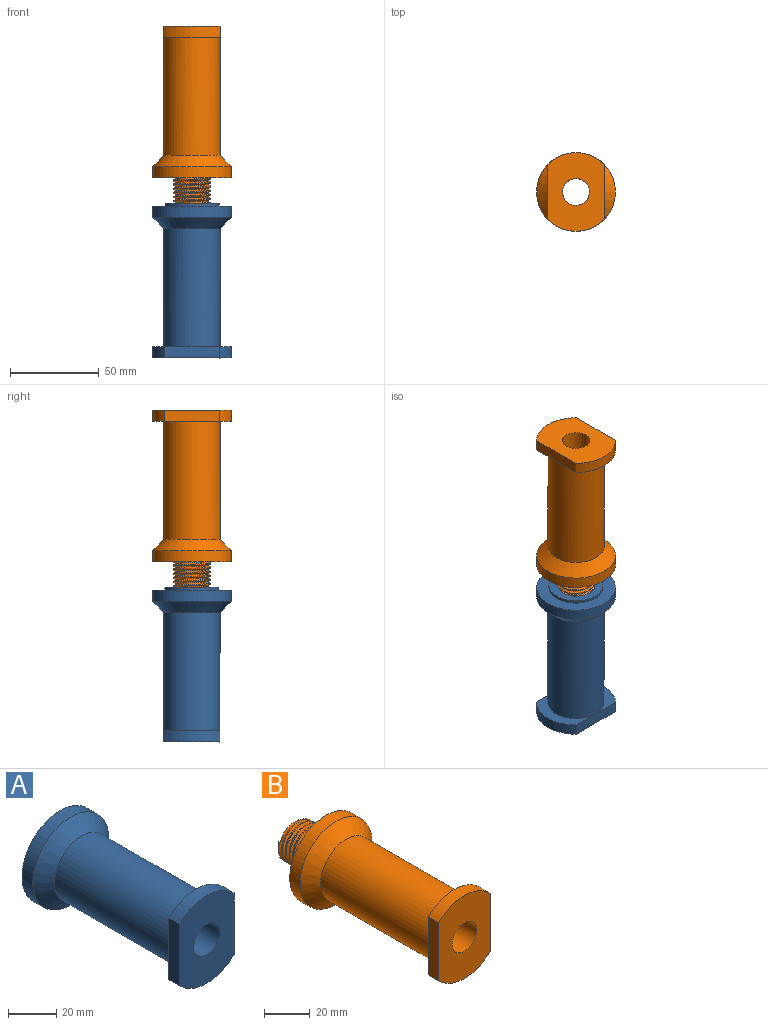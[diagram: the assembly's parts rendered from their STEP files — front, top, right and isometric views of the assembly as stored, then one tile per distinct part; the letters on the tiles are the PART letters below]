
ASSEMBLY  parts=2 mates=1
PART A: 34 faces, bbox 45x87.8x45 mm
  f0: plane 20.7x14.09mm, normal (0,1,0), area 25.9mm2, adj f1,f2,f3,f4,f17
  f1: bspline ~28.83x23.46mm, area 930.4mm2, adj f0,f2,f3,f5,f17,f18,f19,f20
  f2: plane 0.98x0.58mm, normal (0.98,0,0.17), area 0.3mm2, adj f0,f1,f17
  f3: cylinder r=9.06mm len=27.88mm, axis (0,1,0), area 343.1mm2, adj f0,f1,f4,f30
  f4: bspline ~28.07x23.46mm, area 907.7mm2, adj f0,f3,f17,f18,f19,f20,f21,f22
  f5: plane 20.32x20.32mm, normal (0,1,0), area 134.2mm2, adj f1,f7,f29,f30
  f6: cylinder r=15.88mm len=66.68mm, axis (0,1,0), area 6650.5mm2, adj f10,f11,f31
  f7: cylinder r=7.62mm len=57.79mm, axis (0,1,0), area 2766.6mm2, adj f5,f16
  f8: plane 44.45x44.45mm, normal (0,1,0), area 822.1mm2, adj f9,f32
  f9: cylinder r=22.23mm len=44.45mm, axis (0,1,0), area 886.7mm2, adj f8,f31
  f10: plane 31.75x22.23mm, normal (0,1,0), area 244mm2, adj f6,f12,f13,f14
  f11: plane 31.75x22.23mm, normal (0,1,0), area 244mm2, adj f6,f12,f14,f15
  f12: plane 31.11x6.35mm, normal (1,0,0), area 197.5mm2, adj f10,f11,f13,f15,f16
  f13: cylinder r=22.23mm len=31.75mm, axis (0,1,0), area 224.6mm2, adj f10,f12,f14,f16
  f14: plane 31.11x6.35mm, normal (-1,0,0), area 197.5mm2, adj f10,f11,f13,f15,f16
  f15: cylinder r=22.23mm len=31.75mm, axis (0,1,0), area 224.6mm2, adj f11,f12,f14,f16
  f16: plane 44.45x31.75mm, normal (0,-1,0), area 1097.4mm2, adj f7,f12,f13,f14,f15
  f17: cylinder r=10.16mm len=20.32mm, axis (0,1,0), area 120.9mm2, adj f0,f1,f2,f4,f18,f33
  f18: cylinder r=10.16mm len=20.32mm, axis (0,1,0), area 32.4mm2, adj f1,f4,f17,f19
  f19: cylinder r=10.16mm len=20.32mm, axis (0,1,0), area 32.4mm2, adj f1,f4,f18,f20
  f20: cylinder r=10.16mm len=20.32mm, axis (0,1,0), area 32.4mm2, adj f1,f4,f19,f21
  f21: cylinder r=10.16mm len=20.32mm, axis (0,1,0), area 32.4mm2, adj f1,f4,f20,f22
  f22: cylinder r=10.16mm len=20.32mm, axis (0,1,0), area 32.5mm2, adj f1,f4,f21,f23
  f23: cylinder r=10.16mm len=20.32mm, axis (0,1,0), area 32.5mm2, adj f1,f4,f22,f24
  f24: cylinder r=10.16mm len=20.32mm, axis (0,1,0), area 32.4mm2, adj f1,f4,f23,f25
  f25: cylinder r=10.16mm len=20.32mm, axis (0,1,0), area 32.4mm2, adj f1,f4,f24,f26
  f26: cylinder r=10.16mm len=20.32mm, axis (0,1,0), area 32.4mm2, adj f1,f4,f25,f27
  f27: cylinder r=10.16mm len=20.32mm, axis (0,1,0), area 32.4mm2, adj f1,f4,f26,f28
  f28: cylinder r=10.16mm len=20.32mm, axis (0,1,0), area 32.5mm2, adj f1,f4,f27,f29
  f29: cylinder r=10.16mm len=20.32mm, axis (0,1,0), area 41mm2, adj f1,f5,f28,f30
  f30: plane 1.21x1.1mm, normal (0,0,-1), area 1mm2, adj f1,f3,f4,f5,f29
  f31: cone r=15.88mm half-angle=45deg, axis (0,1,0), area 1074.9mm2, adj f6,f9
  f32: cylinder r=15.24mm len=30.48mm, axis (0,-1,0), area 145.9mm2, adj f8,f33
  f33: plane 30.48x30.48mm, normal (0,1,0), area 405.4mm2, adj f17,f32
PART B: 21 faces, bbox 45x106.2x45 mm
  f0: bspline ~99.31x24.54mm, area 3452.3mm2, adj f1,f2,f14,f16,f18,f19
  f1: plane 1.21x1.04mm, normal (0.34,0,0.94), area 1mm2, adj f0,f2,f16,f19,f20
  f2: cylinder r=9.53mm len=98.43mm, axis (0,1,0), area 3108.6mm2, adj f0,f1,f14,f16,f18,f20
  f3: cylinder r=10.79mm len=79.38mm, axis (0,1,0), area 5383.8mm2, adj f5,f14
  f4: cylinder r=15.88mm len=66.68mm, axis (0,1,0), area 6650.5mm2, adj f7,f8,f17
  f5: plane 44.45x44.45mm, normal (0,1,0), area 1185.7mm2, adj f3,f6
  f6: cylinder r=22.23mm len=44.45mm, axis (0,1,0), area 886.7mm2, adj f5,f17
  f7: plane 31.75x22.23mm, normal (0,1,0), area 244mm2, adj f4,f9,f10,f11
  f8: plane 31.75x22.23mm, normal (0,1,0), area 244mm2, adj f4,f9,f11,f12
  f9: plane 31.11x6.35mm, normal (1,0,0), area 197.5mm2, adj f7,f8,f10,f12,f13
  f10: cylinder r=22.23mm len=31.75mm, axis (0,1,0), area 224.6mm2, adj f7,f9,f11,f13
  f11: plane 31.11x6.35mm, normal (-1,0,0), area 197.5mm2, adj f7,f8,f10,f12,f13
  f12: cylinder r=22.23mm len=31.75mm, axis (0,1,0), area 224.6mm2, adj f8,f9,f11,f13
  f13: plane 44.45x31.75mm, normal (0,-1,0), area 1097.4mm2, adj f9,f10,f11,f12,f15
  f14: plane 22.14x22.14mm, normal (0,1,0), area 54.3mm2, adj f0,f2,f3,f18,f19,f20
  f15: cylinder r=7.62mm len=104.78mm, axis (0,1,0), area 5016.4mm2, adj f13,f16
  f16: plane 19.84x19.05mm, normal (0,1,0), area 110.3mm2, adj f0,f1,f2,f15
  f17: cone r=15.88mm half-angle=45deg, axis (0,1,0), area 1074.9mm2, adj f4,f6
  f18: plane 0.99x0.57mm, normal (0,0,-1), area 0.3mm2, adj f0,f2,f14
  f19: cylinder r=10.62mm len=98.36mm, axis (0,1,0), area -1280.3mm2, adj f0,f1,f14,f20
  f20: bspline ~98.93x24.54mm, area 3438mm2, adj f1,f2,f14,f19
PLACE A rot(axis=(0.58,0.58,0.58),120deg) t=(81.48,79.38,118.14)mm fixed
PLACE B rot(axis=(0,-0.71,0.71),180deg) t=(81.48,79.36,134.02)mm
MATE cylindrical A.f3 <-> B.f2  axis (0,0,1) through (81.48,79.38,114.97)mm
